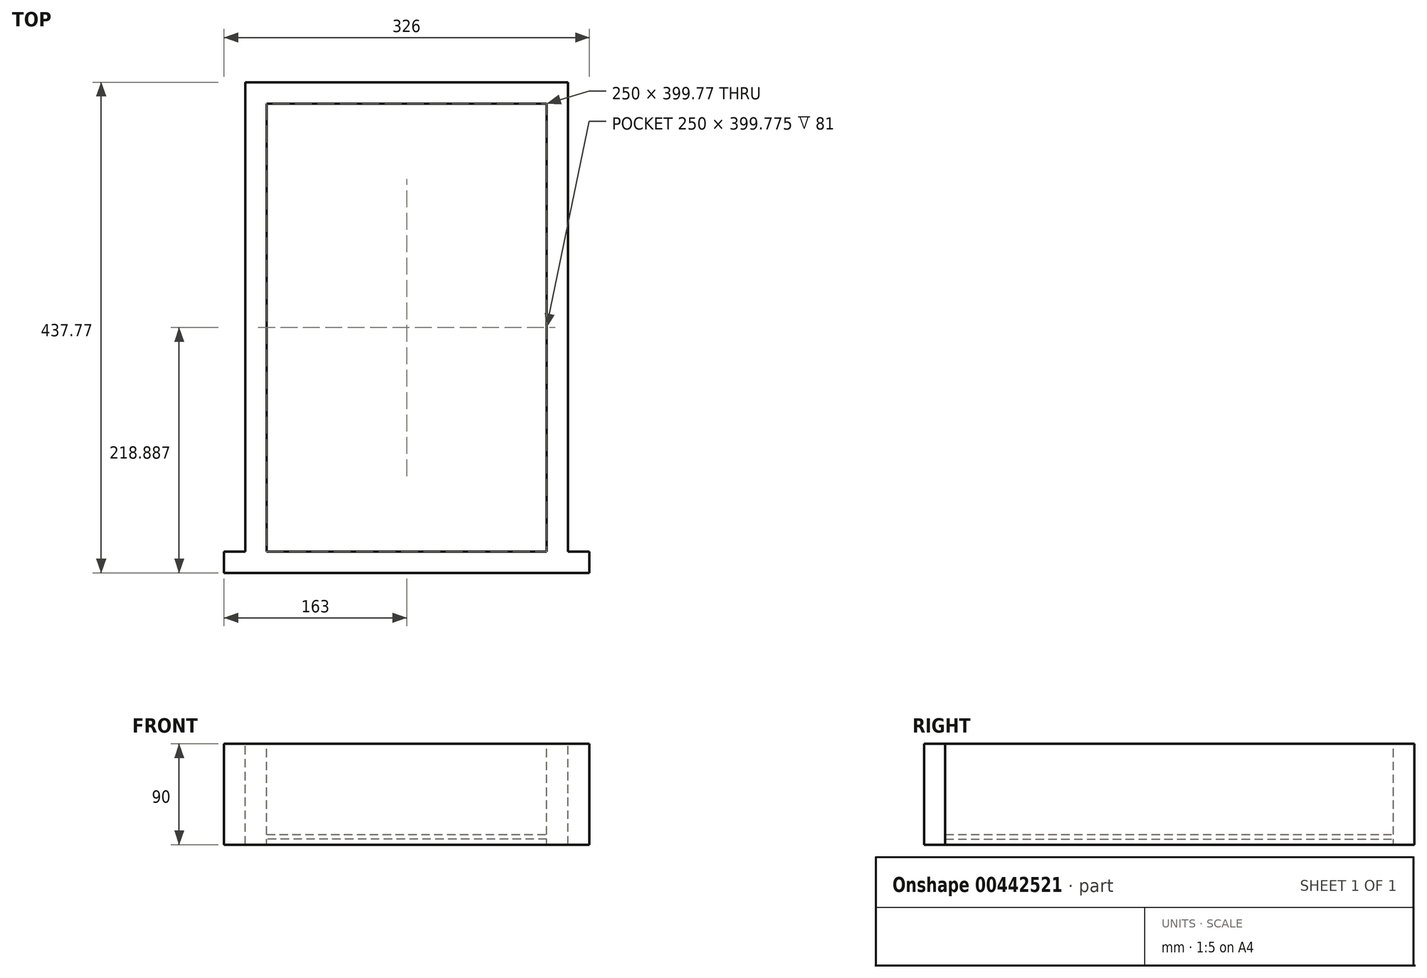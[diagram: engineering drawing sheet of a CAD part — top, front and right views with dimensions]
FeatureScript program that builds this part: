
annotation { "Feature Type Name" : "Feature", "Feature Type Description" : "" }
export const myFeature = defineFeature(function(context is Context, id is Id, definition is map)
    precondition{}
    {
        {
            var Q0;
            Q0=qCreatedBy(makeId("Top.planeOp"),FACE);
            var sketch = newSketch(context, id + "F0", { "sketchPlane" : qUnion([Q0])});
            skLineSegment(sketch, "E0.bottom", {"start": v(0, 0) * mm, "end": v(-288, 0) * mm});
            skLineSegment(sketch, "E0.left", {"start": v(0, 19) * mm, "end": v(0, 437.77) * mm});
            skLineSegment(sketch, "E0.right", {"start": v(-288, 19) * mm, "end": v(-288, 437.77) * mm});
            skLineSegment(sketch, "E1.1", {"start": v(-19, 19) * mm, "end": v(-19, 418.77) * mm});
            skLineSegment(sketch, "E1.3", {"start": v(-269, 19) * mm, "end": v(-269, 418.77) * mm});
            skLineSegment(sketch, "E2", {"start": v(-288, 19) * mm, "end": v(-307, 19) * mm});
            skLineSegment(sketch, "E3", {"start": v(-307, 19) * mm, "end": v(-307, 0) * mm});
            skLineSegment(sketch, "E4", {"start": v(-307, 0) * mm, "end": v(-288, 0) * mm});
            skLineSegment(sketch, "E5", {"start": v(19, 15.77) * mm, "end": v(19, 0) * mm});
            skLineSegment(sketch, "E6", {"start": v(19, 0) * mm, "end": v(0, 0) * mm});
            skLineSegment(sketch, "E7", {"start": v(-288, 437.77) * mm, "end": v(0, 437.77) * mm});
            skLineSegment(sketch, "E8", {"start": v(0, 437.77) * mm, "end": v(0, 418.77) * mm});
            skLineSegment(sketch, "E9", {"start": v(-19, 418.77) * mm, "end": v(-269, 418.77) * mm});
            skPoint(sketch, "E10.end.orphan", {"position": v(0, 447.77) * mm});
            skLineSegment(sketch, "E11", {"start": v(-269, 19) * mm, "end": v(-19, 19) * mm});
            skLineSegment(sketch, "E12", {"start": v(0, 19) * mm, "end": v(19, 19) * mm});
            skLineSegment(sketch, "E13", {"start": v(19, 19) * mm, "end": v(19, 15.77) * mm});
            skPoint(sketch, "E14.orphan", {"position": v(0, 15.77) * mm});
            skPoint(sketch, "E1.2.start.orphan", {"position": v(-19, 15.77) * mm});
            skPoint(sketch, "E15.orphan", {"position": v(-269, 15.77) * mm});
            skSolve(sketch);
        }
        {
            var Q0;
            Q0 = qSketchRegion(id + "F0", true);
            extrude(context, id + "F1", {"entities" : qUnion([Q0]), "oppositeDirection" : true, "depth" : 90 * mm});
        }
        {
            var Q0;
            Q0=qCreatedBy(makeId("Top.planeOp"),FACE);
            cPlane(context, id + "F2", {"entities" : qUnion([Q0]), "cplaneType" : CPlaneType.OFFSET, "offset" : 85 * mm, "oppositeDirection" : true, "width" : 150 * mm, "height" : 150 * mm});
        }
        {
            var Q0;
            Q0=qCreatedBy(id+"F2.planeOp",FACE);
            var sketch = newSketch(context, id + "F3", { "sketchPlane" : qUnion([Q0])});
            skLineSegment(sketch, "E16", {"start": v(0, 0) * mm, "end": v(0, 19) * mm, "construction": true});
            skLineSegment(sketch, "E17", {"start": v(0, 19) * mm, "end": v(-19, 19) * mm, "construction": true});
            skLineSegment(sketch, "E18.0", {"start": v(-19, 19) * mm, "end": v(-19, 19) * mm});
            skLineSegment(sketch, "E18.2", {"start": v(-269, 19) * mm, "end": v(-269, 19) * mm});
            skLineSegment(sketch, "E19.0", {"start": v(-269, 432) * mm, "end": v(-19, 432) * mm});
            skLineSegment(sketch, "E19.1", {"start": v(-19, 19) * mm, "end": v(-19, 432) * mm});
            skLineSegment(sketch, "E19.2", {"start": v(-269, 19) * mm, "end": v(-269, 432) * mm});
            skLineSegment(sketch, "E19.3", {"start": v(-19, 19) * mm, "end": v(-269, 19) * mm});
            skSolve(sketch);
        }
        {
            var Q0;
            Q0 = qSketchRegion(id + "F3", true);
            extrude(context, id + "F4", {"entities" : qUnion([Q0]), "operationType" : NewBodyOperationType.ADD, "depth" : 4 * mm});
        }
    });
